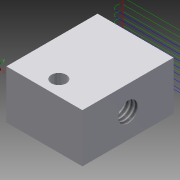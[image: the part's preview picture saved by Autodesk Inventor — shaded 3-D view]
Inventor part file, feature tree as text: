
AUTODESK INVENTOR PART (.ipt)
format: ipt  version: 2015 SP1 (Build 190203100, 203)  size: 190,976 bytes
history: native  units: in
note: dims shown in document units (in); Inventor stores cm internally (conversion verified against a paired STEP export)
features: hole x2, extrude x1, sketch x1
ambient origin geometry x8: Origin, YZ Plane, XZ Plane, XY Plane, X Axis, Y Axis, Z Axis, Center Point
bodies: Solid1 (feature_tree)
feature tree (4):
  extrude  "Extrusion1"  [1 undecoded]
  hole  "Hole1"  [1 undecoded]
  hole  "Hole2"  [1 undecoded]
  sketch  "Sketch1"  dims[d2=0.0in d3=0.0984in d4=0.2411in d5=0.0968in d6=0.2362in d7=0.1575in d8=0.0787in d9=90.0deg d10=0.315in d11=0.8108in d12=0.2953in d13=0.1575in d14=0.1276in d15=0.315in d16=0.1575in d17=0.0787in d18=90.0deg d19=0.4646in d20=0.8108in]
note: 3 required parameter values undecoded (feature->parameter linkage not recoverable at this tier; creation-order binding heuristic only, values carry confidence <= 0.55)
